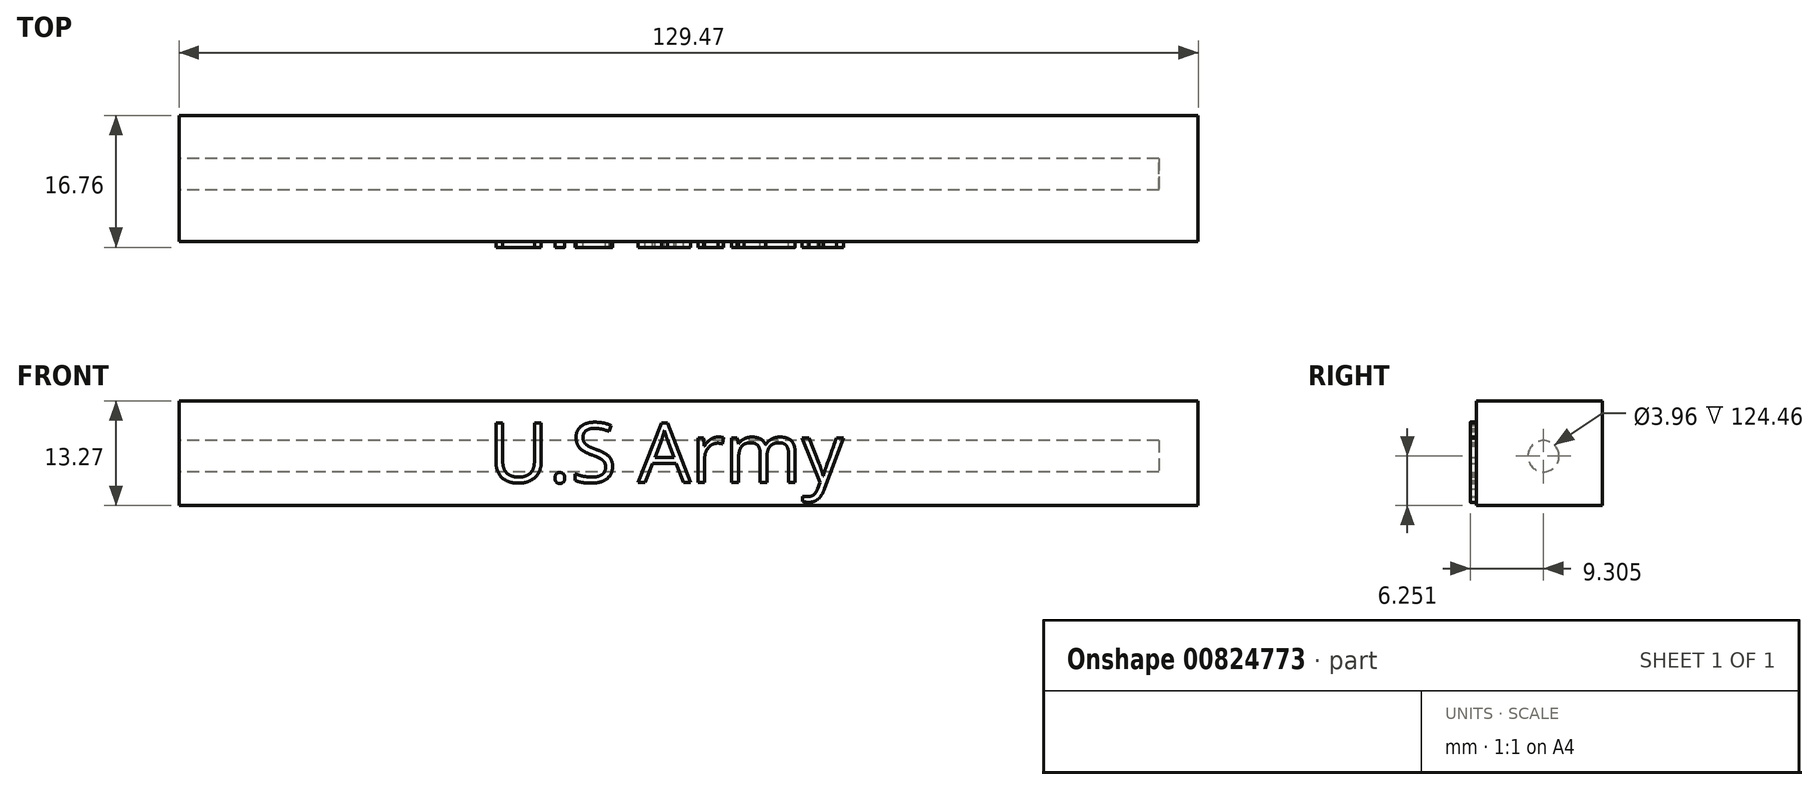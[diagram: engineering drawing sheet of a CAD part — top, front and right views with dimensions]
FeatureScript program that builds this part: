
annotation { "Feature Type Name" : "Feature", "Feature Type Description" : "" }
export const myFeature = defineFeature(function(context is Context, id is Id, definition is map)
    precondition{}
    {
        {
            var Q0;
            Q0=qCreatedBy(makeId("Front.planeOp"),FACE);
            var sketch = newSketch(context, id + "F0", { "sketchPlane" : qUnion([Q0])});
            skLineSegment(sketch, "E0.bottom", {"start": v(-52.8, 13.27) * mm, "end": v(76.67, 13.27) * mm});
            skLineSegment(sketch, "E0.top", {"start": v(-52.8, 0) * mm, "end": v(76.67, 0) * mm});
            skLineSegment(sketch, "E0.left", {"start": v(-52.8, 13.27) * mm, "end": v(-52.8, 0) * mm});
            skLineSegment(sketch, "E0.right", {"start": v(76.67, 13.27) * mm, "end": v(76.67, 0) * mm});
            skSolve(sketch);
        }
        {
            var Q0;
            Q0 = qSketchRegion(id + "F0", true);
            extrude(context, id + "F1", {"entities" : qUnion([Q0]), "depth" : 16 * mm, "offsetDistance" : 25.4 * mm});
        }
        {
            var Q0;
            Q0=makeQuery(id+"F1.opExtrude","SWEPT_FACE",FACE,{"disambiguationData":[OSD([sQuery(id+"F0.wireOp",EDGE,"E0.left")])]});
            var sketch = newSketch(context, id + "F2", { "sketchPlane" : qUnion([Q0])});
            skCircle(sketch, "E1", {"center": v(7.46, 6.25) * mm, "radius": 1.98 * mm});
            skSolve(sketch);
        }
        {
            var Q0;
            Q0=makeQuery(id+"F2.imprint","IMPRINT",FACE,{"disambiguationData":[TD([[makeQuery(id+"F2.imprint","IMPRINT",EDGE,{"derivedFrom":sQuery(id+"F2.wireOp",EDGE,"E1")}),1.0]])]});
            extrude(context, id + "F3", {"entities" : qUnion([Q0]), "operationType" : NewBodyOperationType.REMOVE, "oppositeDirection" : true, "depth" : 124.46 * mm, "offsetDistance" : 25.4 * mm});
        }
        {
            var Q0;
            Q0=makeQuery(id+"F1.opExtrude","CAP_FACE",FACE,{"disambiguationData":[OSD([sQuery(id+"F0.wireOp",EDGE,"E0.bottom"),sQuery(id+"F0.wireOp",EDGE,"E0.top"),sQuery(id+"F0.wireOp",EDGE,"E0.left"),sQuery(id+"F0.wireOp",EDGE,"E0.right")])],"isStart":false});
            var sketch = newSketch(context, id + "F4", { "sketchPlane" : qUnion([Q0])});
            skText(sketch, "E2", { "text": "U.S Army \n", "fontName": "OpenSans-Regular.ttf"});
            const initialGuessF4  = {"E2": [-0.0135, 0.00293, 1, 0, 0.0076]};
            skSetInitialGuess(sketch, initialGuessF4);
            skSolve(sketch);
        }
        {
            var Q0;
            Q0 = qSketchRegion(id + "F4", true);
            extrude(context, id + "F5", {"entities" : qUnion([Q0]), "operationType" : NewBodyOperationType.ADD, "depth" : 0.76 * mm, "offsetDistance" : 25.4 * mm});
        }
    });
